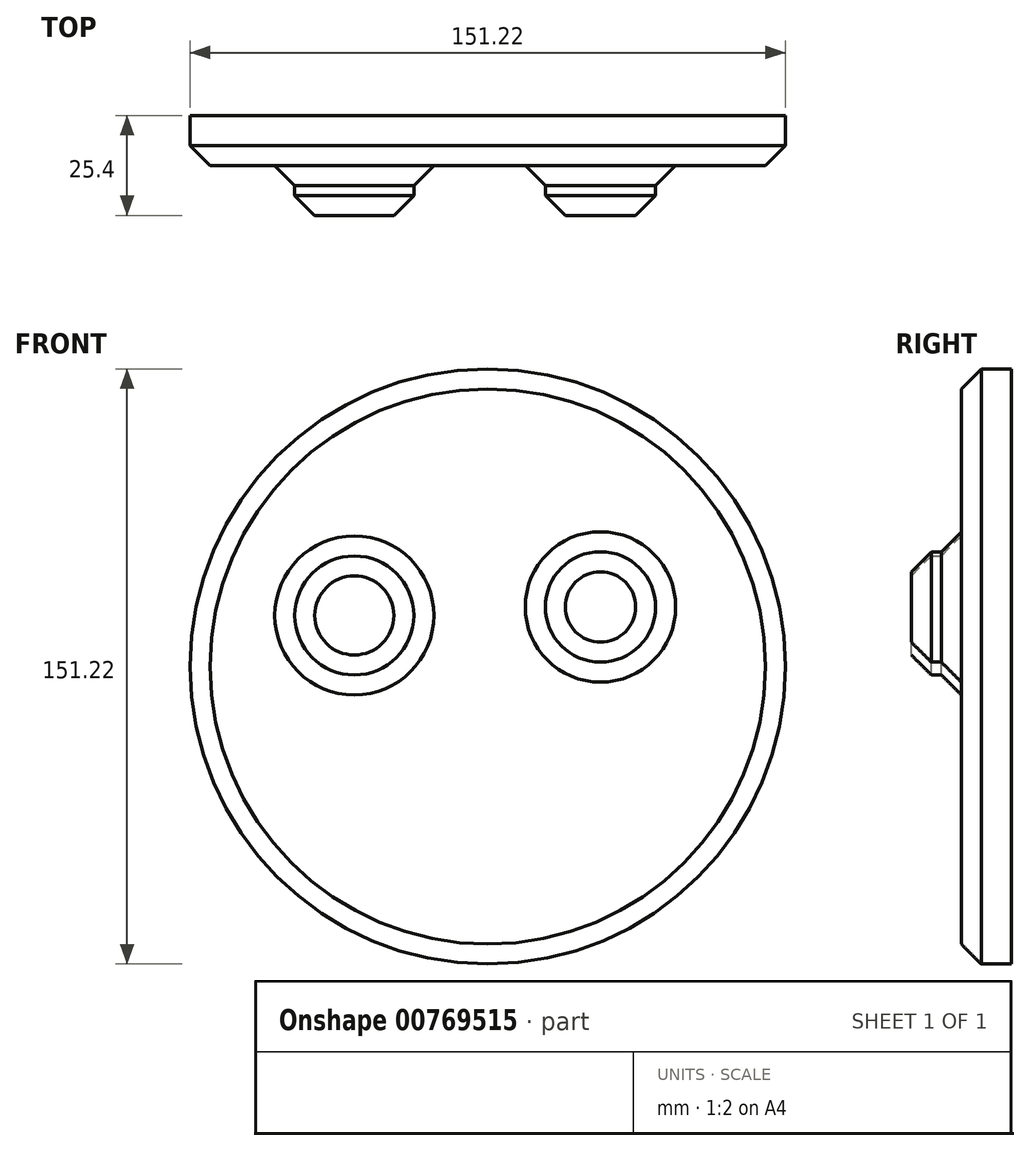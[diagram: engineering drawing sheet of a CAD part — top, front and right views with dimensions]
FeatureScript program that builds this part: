
annotation { "Feature Type Name" : "Feature", "Feature Type Description" : "" }
export const myFeature = defineFeature(function(context is Context, id is Id, definition is map)
    precondition{}
    {
        {
            var Q0;
            Q0=qCreatedBy(makeId("Front.planeOp"),FACE);
            var sketch = newSketch(context, id + "F0", { "sketchPlane" : qUnion([Q0])});
            skCircle(sketch, "E0", {"center": v(0, 0) * mm, "radius": 75.61 * mm});
            skSolve(sketch);
        }
        {
            var Q0;
            Q0 = qSketchRegion(id + "F0", true);
            extrude(context, id + "F1", {"entities" : qUnion([Q0]), "depth" : 12.7 * mm, "offsetDistance" : 25.4 * mm});
        }
        {
            var Q0;
            Q0=makeQuery(id+"F1.opExtrude","CAP_FACE",FACE,{"disambiguationData":[OSD([sQuery(id+"F0.wireOp",EDGE,"E0")])],"isStart":false});
            var sketch = newSketch(context, id + "F2", { "sketchPlane" : qUnion([Q0])});
            skCircle(sketch, "E1", {"center": v(28.64, 15.14) * mm, "radius": 14.02 * mm});
            skCircle(sketch, "E2", {"center": v(-33.9, 12.96) * mm, "radius": 15.13 * mm});
            skSolve(sketch);
        }
        {
            var Q0;
            Q0 = qSketchRegion(id + "F2", true);
            extrude(context, id + "F3", {"entities" : qUnion([Q0]), "operationType" : NewBodyOperationType.ADD, "depth" : 12.7 * mm, "offsetDistance" : 25.4 * mm});
        }
        {
            var Q0;
            Q0=makeQuery(id+"F3.opExtrude","CAP_FACE",FACE,{"disambiguationData":[OSD([sQuery(id+"F2.wireOp",EDGE,"E2")])],"isStart":false});
            var Q1;
            Q1=makeQuery(id+"F3.opExtrude","CAP_FACE",FACE,{"disambiguationData":[OSD([sQuery(id+"F2.wireOp",EDGE,"E1")])],"isStart":false});
            chamfer(context, id + "F4", {"entities" : qUnion([Q0, Q1]), "width" : 5.08 * mm, "tangentPropagation" : true});
        }
        {
            var Q0;
            Q0=makeQuery(id+"F1.opExtrude","CAP_FACE",FACE,{"disambiguationData":[OSD([sQuery(id+"F0.wireOp",EDGE,"E0")])],"isStart":false});
            chamfer(context, id + "F5", {"entities" : qUnion([Q0]), "width" : 5.08 * mm, "tangentPropagation" : true});
        }
    });
